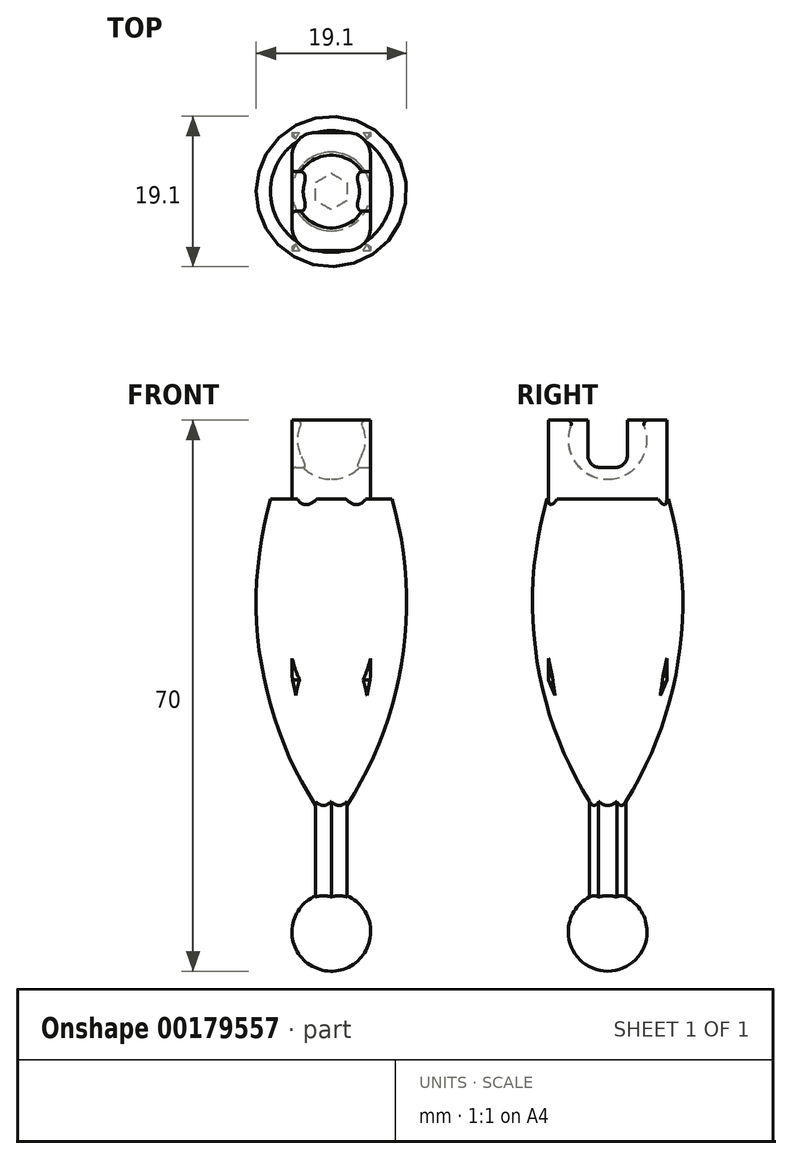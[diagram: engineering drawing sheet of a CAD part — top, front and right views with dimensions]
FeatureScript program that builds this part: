
annotation { "Feature Type Name" : "Feature", "Feature Type Description" : "" }
export const myFeature = defineFeature(function(context is Context, id is Id, definition is map)
    precondition{}
    {
        {
            var Q0;
            Q0=qCreatedBy(makeId("Right.planeOp"),FACE);
            var sketch = newSketch(context, id + "F0", { "sketchPlane" : qUnion([Q0])});
            skLineSegment(sketch, "E0.bottom", {"start": v(-7.5, 60.25) * mm, "end": v(7.5, 60.25) * mm});
            skLineSegment(sketch, "E0.top", {"start": v(-7.5, 15.25) * mm, "end": v(7.5, 15.25) * mm});
            skLineSegment(sketch, "E0.left", {"start": v(-7.5, 60.25) * mm, "end": v(-7.5, 15.25) * mm});
            skLineSegment(sketch, "E0.right", {"start": v(7.5, 60.25) * mm, "end": v(7.5, 15.25) * mm});
            skSolve(sketch);
        }
        {
            var Q0;
            Q0=qSketchRegion(id+"F0",true);
            extrude(context, id + "F1", {"entities" : qUnion([Q0]), "endBound" : BoundingType.SYMMETRIC, "depth" : 10 * mm});
        }
        {
            var Q0;
            Q0=makeQuery(id+"F1.opExtrude","CAP_FACE",FACE,{"disambiguationData":[OSD([sQuery(id+"F0.wireOp",EDGE,"E0.bottom"),sQuery(id+"F0.wireOp",EDGE,"E0.top"),sQuery(id+"F0.wireOp",EDGE,"E0.left"),sQuery(id+"F0.wireOp",EDGE,"E0.right")])],"isStart":false});
            var sketch = newSketch(context, id + "F2", { "sketchPlane" : qUnion([Q0])});
            skLineSegment(sketch, "E1", {"start": v(-7.5, 15.25) * mm, "end": v(-7.5, 27.25) * mm});
            skLineSegment(sketch, "E2", {"start": v(-7.5, 27.25) * mm, "end": v(-2.5, 15.25) * mm});
            skLineSegment(sketch, "E3", {"start": v(-2.5, 15.25) * mm, "end": v(-7.5, 15.25) * mm});
            skLineSegment(sketch, "E4", {"start": v(0, 60.25) * mm, "end": v(0, 15.25) * mm, "construction": true});
            skLineSegment(sketch, "E5.MirrorCS", {"start": v(7.5, 15.25) * mm, "end": v(7.5, 27.25) * mm});
            skLineSegment(sketch, "E6.MirrorCS", {"start": v(7.5, 27.25) * mm, "end": v(2.5, 15.25) * mm});
            skLineSegment(sketch, "E7.MirrorCS", {"start": v(2.5, 15.25) * mm, "end": v(7.5, 15.25) * mm});
            skSolve(sketch);
        }
        {
            var Q0;
            Q0=qSketchRegion(id+"F2",true);
            extrude(context, id + "F3", {"entities" : qUnion([Q0]), "operationType" : NewBodyOperationType.REMOVE, "endBound" : BoundingType.SYMMETRIC, "oppositeDirection" : true, "depth" : 25 * mm});
        }
        {
            var Q0;
            Q0=qCreatedBy(makeId("Front.planeOp"),FACE);
            var sketch = newSketch(context, id + "F4", { "sketchPlane" : qUnion([Q0])});
            skLineSegment(sketch, "E8", {"start": v(5, 27.75) * mm, "end": v(5, 15.25) * mm});
            skLineSegment(sketch, "E9", {"start": v(5, 15.25) * mm, "end": v(2.5, 15.25) * mm});
            skLineSegment(sketch, "E10", {"start": v(2.5, 15.25) * mm, "end": v(5, 27.75) * mm});
            skLineSegment(sketch, "E11", {"start": v(0, 10.16) * mm, "end": v(0, 28) * mm, "construction": true});
            skLineSegment(sketch, "E12.MirrorCS", {"start": v(-5, 27.75) * mm, "end": v(-5, 15.25) * mm});
            skLineSegment(sketch, "E13.MirrorCS", {"start": v(-5, 15.25) * mm, "end": v(-2.5, 15.25) * mm});
            skLineSegment(sketch, "E14.MirrorCS", {"start": v(-2.5, 15.25) * mm, "end": v(-5, 27.75) * mm});
            skSolve(sketch);
        }
        {
            var Q0;
            Q0=qSketchRegion(id+"F4",true);
            extrude(context, id + "F5", {"entities" : qUnion([Q0]), "operationType" : NewBodyOperationType.REMOVE, "endBound" : BoundingType.SYMMETRIC, "oppositeDirection" : true, "depth" : 50 * mm});
        }
        {
            var Q0;
            Q0=makeQuery(id+"F1.opExtrude","SWEPT_FACE",FACE,{"disambiguationData":[OSD([sQuery(id+"F0.wireOp",EDGE,"E0.top")])]});
            var sketch = newSketch(context, id + "F6", { "sketchPlane" : qUnion([Q0])});
            skCircle(sketch, "E15.cCircle", {"center": v(0, 0) * mm, "radius": 2 * mm, "construction": true});
            skPoint(sketch, "E15.cCircle.perimeterSnap0", {"position": v(2.5, 0) * mm});
            skPoint(sketch, "E15.cCircle.perimeterSnap1", {"position": v(2.09, 0.04) * mm});
            skLineSegment(sketch, "E15.0", {"start": v(2, 1.15) * mm, "end": v(2, -1.15) * mm});
            skLineSegment(sketch, "E15.1", {"start": v(2, -1.15) * mm, "end": v(0, -2.3) * mm});
            skLineSegment(sketch, "E15.2", {"start": v(0, -2.3) * mm, "end": v(-2, -1.15) * mm});
            skLineSegment(sketch, "E15.3", {"start": v(-2, -1.15) * mm, "end": v(-2, 1.15) * mm});
            skLineSegment(sketch, "E15.4", {"start": v(-2, 1.15) * mm, "end": v(0, 2.3) * mm});
            skLineSegment(sketch, "E15.5", {"start": v(0, 2.3) * mm, "end": v(2, 1.15) * mm});
            skPoint(sketch, "E15.0.midPoint", {"position": v(2.09, 0) * mm});
            skPoint(sketch, "E15.0.midPoint.positionSnap0", {"position": v(2.5, 0) * mm});
            skPoint(sketch, "E15.0.midPoint.positionSnap1", {"position": v(2.09, 0.04) * mm});
            skSolve(sketch);
        }
        {
            var Q0;
            Q0=qSketchRegion(id+"F6",true);
            extrude(context, id + "F7", {"entities" : qUnion([Q0]), "operationType" : NewBodyOperationType.ADD, "depth" : 20 * mm});
        }
        {
            var Q0;
            Q0=makeQuery(id+"F7.opExtrude","CAP_FACE",FACE,{"disambiguationData":[OSD([sQuery(id+"F6.wireOp",EDGE,"E15.0"),sQuery(id+"F6.wireOp",EDGE,"E15.1"),sQuery(id+"F6.wireOp",EDGE,"E15.2"),sQuery(id+"F6.wireOp",EDGE,"E15.3"),sQuery(id+"F6.wireOp",EDGE,"E15.4"),sQuery(id+"F6.wireOp",EDGE,"E15.5")])],"isStart":false});
            var sketch = newSketch(context, id + "F8", { "sketchPlane" : qUnion([Q0])});
            skArc(sketch, "E16", {"start": v(0, 5) * mm, "mid": v(-5, 0) * mm, "end": v(0, -5) * mm});
            skLineSegment(sketch, "E17", {"start": v(0, 5) * mm, "end": v(0, -5) * mm});
            skLineSegment(sketch, "E18", {"start": v(0, 6.34) * mm, "end": v(0, -6.26) * mm, "construction": true});
            skSolve(sketch);
        }
        {
            var Q0;
            {var subQ2=sQuery(id+"F8.wireOp",EDGE,"E16");Q0=makeQuery(id+"F8.imprint","IMPRINT",FACE,{"disambiguationData":[TD([[makeQuery(id+"F8.imprint","IMPRINT",EDGE,{"derivedFrom":subQ2}),1.0]])]});}
            var Q1;
            {var subQ1=makeQuery(id+"F7.opExtrude","CAP_EDGE",EDGE,{"disambiguationData":[OSD([sQuery(id+"F6.wireOp",EDGE,"E15.2")])],"isStart":false});Q1=makeQuery(id+"F8.imprint","IMPRINT",FACE,{"disambiguationData":[TD([[makeQuery(id+"F8.imprint","IMPRINT",EDGE,{"derivedFrom":subQ1}),-1.0]])]});}
            var Q2;
            Q2=sQuery(id+"F8.wireOp",EDGE,"E18");
            revolve(context, id + "F9", {"operationType" : NewBodyOperationType.ADD, "entities" : qUnion([Q0, Q1]), "axis" : qUnion([Q2]), "revolveType" : RevolveType.FULL});
        }
        {
            var Q0;
            Q0=makeQuery(id+"F1.opExtrude","CAP_FACE",FACE,{"disambiguationData":[OSD([sQuery(id+"F0.wireOp",EDGE,"E0.bottom"),sQuery(id+"F0.wireOp",EDGE,"E0.top"),sQuery(id+"F0.wireOp",EDGE,"E0.left"),sQuery(id+"F0.wireOp",EDGE,"E0.right")])],"isStart":false});
            var sketch = newSketch(context, id + "F10", { "sketchPlane" : qUnion([Q0])});
            skLineSegment(sketch, "E19.bottom", {"start": v(-2.5, 60.25) * mm, "end": v(2.5, 60.25) * mm});
            skLineSegment(sketch, "E19.top", {"start": v(-1, 54.25) * mm, "end": v(1, 54.25) * mm});
            skLineSegment(sketch, "E19.left", {"start": v(-2.5, 60.25) * mm, "end": v(-2.5, 55.75) * mm});
            skLineSegment(sketch, "E19.right", {"start": v(2.5, 60.25) * mm, "end": v(2.5, 55.75) * mm});
            skPoint(sketch, "E20.visualSharp", {"position": v(-2.5, 54.25) * mm});
            skArc(sketch, "E20.filletArc", {"start": v(-2.5, 55.75) * mm, "mid": v(-2.06, 54.69) * mm, "end": v(-1, 54.25) * mm});
            skPoint(sketch, "E21.visualSharp", {"position": v(2.5, 54.25) * mm});
            skArc(sketch, "E21.filletArc", {"start": v(1, 54.25) * mm, "mid": v(2.06, 54.69) * mm, "end": v(2.5, 55.75) * mm});
            skSolve(sketch);
        }
        {
            var Q0;
            Q0=qSketchRegion(id+"F10",true);
            extrude(context, id + "F11", {"entities" : qUnion([Q0]), "operationType" : NewBodyOperationType.REMOVE, "endBound" : BoundingType.THROUGH_ALL, "oppositeDirection" : true, "depth" : 25 * mm});
        }
        {
            var Q0;
            Q0=qCreatedBy(makeId("Right.planeOp"),FACE);
            var sketch = newSketch(context, id + "F12", { "sketchPlane" : qUnion([Q0])});
            skLineSegment(sketch, "E22", {"start": v(0, 62.75) * mm, "end": v(0, 52.75) * mm});
            skLineSegment(sketch, "E23", {"start": v(0, 54.58) * mm, "end": v(0, 40) * mm, "construction": true});
            skPoint(sketch, "E24.center.orphan", {"position": v(0, 57.75) * mm});
            skArc(sketch, "E25", {"start": v(0, 62.75) * mm, "mid": v(-5, 57.75) * mm, "end": v(0, 52.75) * mm});
            skSolve(sketch);
        }
        {
            var Q0;
            Q0=qSketchRegion(id+"F12",true);
            var Q1;
            Q1=sQuery(id+"F12.wireOp",EDGE,"E23");
            revolve(context, id + "F13", {"operationType" : NewBodyOperationType.REMOVE, "entities" : qUnion([Q0]), "axis" : qUnion([Q1]), "revolveType" : RevolveType.FULL, "oppositeDirection" : true});
        }
        {
            var Q0;
            Q0=makeQuery(id+"F11.boolean.opBoolean","COPY",EDGE,{"derivedFrom":makeQuery(id+"F11.opExtrude","CAP_EDGE",EDGE,{"disambiguationData":[OSD([sQuery(id+"F10.wireOp",EDGE,"E19.left")])],"isStart":true})});
            var Q1;
            {var subQ0=sQuery(id+"F0.wireOp",EDGE,"E0.bottom");Q1=makeQuery(id+"F13.boolean.opBoolean","INTERSECT",EDGE,{"derivedFrom":[makeQuery(id+"F11.boolean.opBoolean","SPLIT",FACE,{"disambiguationData":[TD([makeQuery(id+"F11.opExtrude","SWEPT_FACE",FACE,{"disambiguationData":[OSD([sQuery(id+"F10.wireOp",EDGE,"E19.right")])]})])],"derivedFrom":makeQuery(id+"F1.opExtrude","SWEPT_FACE",FACE,{"disambiguationData":[OSD([subQ0])]})}),makeQuery(id+"F13.opRevolve","SWEPT_FACE",FACE,{"disambiguationData":[OSD([sQuery(id+"F12.wireOp",EDGE,"E25")])]})]});}
            var Q2;
            {var subQ0=sQuery(id+"F0.wireOp",EDGE,"E0.bottom");Q2=makeQuery(id+"F13.boolean.opBoolean","INTERSECT",EDGE,{"derivedFrom":[makeQuery(id+"F11.boolean.opBoolean","SPLIT",FACE,{"disambiguationData":[TD([makeQuery(id+"F11.opExtrude","SWEPT_FACE",FACE,{"disambiguationData":[OSD([sQuery(id+"F10.wireOp",EDGE,"E19.left")])]})])],"derivedFrom":makeQuery(id+"F1.opExtrude","SWEPT_FACE",FACE,{"disambiguationData":[OSD([subQ0])]})}),makeQuery(id+"F13.opRevolve","SWEPT_FACE",FACE,{"disambiguationData":[OSD([sQuery(id+"F12.wireOp",EDGE,"E25")])]})]});}
            var Q3;
            Q3=makeQuery(id+"F11.boolean.opBoolean","INTERSECT",EDGE,{"derivedFrom":[makeQuery(id+"F1.opExtrude","CAP_FACE",FACE,{"disambiguationData":[OSD([sQuery(id+"F0.wireOp",EDGE,"E0.bottom"),sQuery(id+"F0.wireOp",EDGE,"E0.top"),sQuery(id+"F0.wireOp",EDGE,"E0.left"),sQuery(id+"F0.wireOp",EDGE,"E0.right")])],"isStart":true}),makeQuery(id+"F11.opExtrude","SWEPT_FACE",FACE,{"disambiguationData":[OSD([sQuery(id+"F10.wireOp",EDGE,"E20.filletArc")])]})]});
            fillet(context, id + "F14", {"entities" : qUnion([Q0, Q1, Q2, Q3]), "radius" : 0.5 * mm, "tangentPropagation" : true, "allowEdgeOverflow" : false});
        }
        {
            var Q0;
            Q0=qCreatedBy(makeId("Right.planeOp"),FACE);
            var sketch = newSketch(context, id + "F15", { "sketchPlane" : qUnion([Q0])});
            skArc(sketch, "E26", {"start": v(0, 8.4) * mm, "mid": v(8.75, 28.42) * mm, "end": v(7.73, 50.23) * mm});
            skLineSegment(sketch, "E27", {"start": v(0, 50.23) * mm, "end": v(7.73, 50.23) * mm});
            skLineSegment(sketch, "E28", {"start": v(0, 8.4) * mm, "end": v(0, 50.23) * mm});
            skPoint(sketch, "E29.orphan", {"position": v(0, 65.86) * mm});
            skLineSegment(sketch, "E30", {"start": v(0, 63.33) * mm, "end": v(0, 2.64) * mm, "construction": true});
            skSolve(sketch);
        }
        {
            var Q0;
            Q0 = qSketchRegion(id + "F15", true);
            var Q1;
            Q1=sQuery(id+"F15.wireOp",EDGE,"E30");
            revolve(context, id + "F16", {"operationType" : NewBodyOperationType.ADD, "entities" : qUnion([Q0]), "axis" : qUnion([Q1]), "revolveType" : RevolveType.FULL});
        }
        {
            var Q0;
            {var subQ0=sQuery(id+"F0.wireOp",EDGE,"E0.bottom");var subQ1=sQuery(id+"F0.wireOp",EDGE,"E0.left");Q0=makeQuery(id+"F16.boolean.opBoolean","SPLIT",EDGE,{"disambiguationData":[TD([makeQuery(id+"F1.opExtrude","SWEPT_FACE",FACE,{"disambiguationData":[OSD([subQ0])]})])],"derivedFrom":makeQuery(id+"F1.opExtrude","CAP_EDGE",EDGE,{"disambiguationData":[OSD([subQ1])],"isStart":false})});}
            var Q1;
            {var subQ0=sQuery(id+"F0.wireOp",EDGE,"E0.bottom");var subQ1=sQuery(id+"F0.wireOp",EDGE,"E0.left");Q1=makeQuery(id+"F16.boolean.opBoolean","SPLIT",EDGE,{"disambiguationData":[TD([makeQuery(id+"F1.opExtrude","SWEPT_FACE",FACE,{"disambiguationData":[OSD([subQ0])]})])],"derivedFrom":makeQuery(id+"F1.opExtrude","CAP_EDGE",EDGE,{"disambiguationData":[OSD([subQ1])],"isStart":true})});}
            var Q2;
            {var subQ0=sQuery(id+"F0.wireOp",EDGE,"E0.bottom");var subQ1=sQuery(id+"F0.wireOp",EDGE,"E0.right");Q2=makeQuery(id+"F16.boolean.opBoolean","SPLIT",EDGE,{"disambiguationData":[TD([makeQuery(id+"F1.opExtrude","SWEPT_FACE",FACE,{"disambiguationData":[OSD([subQ0])]})])],"derivedFrom":makeQuery(id+"F1.opExtrude","CAP_EDGE",EDGE,{"disambiguationData":[OSD([subQ1])],"isStart":false})});}
            var Q3;
            {var subQ0=sQuery(id+"F0.wireOp",EDGE,"E0.bottom");var subQ1=sQuery(id+"F0.wireOp",EDGE,"E0.right");Q3=makeQuery(id+"F16.boolean.opBoolean","SPLIT",EDGE,{"disambiguationData":[TD([makeQuery(id+"F1.opExtrude","SWEPT_FACE",FACE,{"disambiguationData":[OSD([subQ0])]})])],"derivedFrom":makeQuery(id+"F1.opExtrude","CAP_EDGE",EDGE,{"disambiguationData":[OSD([subQ1])],"isStart":true})});}
            fillet(context, id + "F17", {"entities" : qUnion([Q0, Q1, Q2, Q3]), "radius" : 3 * mm, "tangentPropagation" : true, "allowEdgeOverflow" : false});
        }
    });
